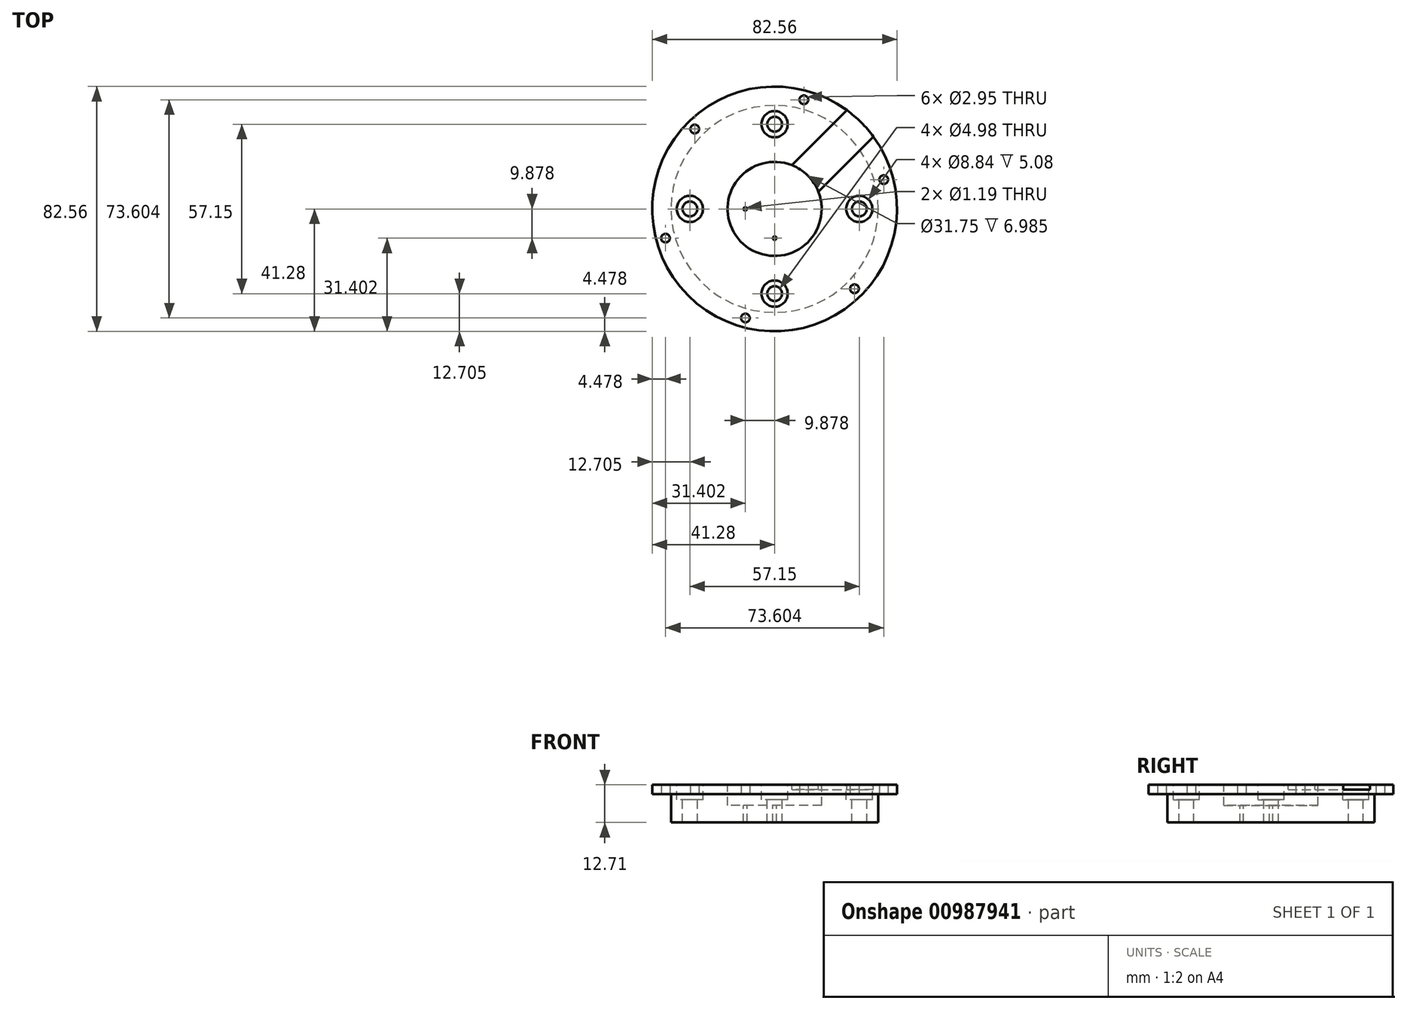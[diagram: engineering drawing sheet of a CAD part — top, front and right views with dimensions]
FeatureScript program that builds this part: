
annotation { "Feature Type Name" : "Feature", "Feature Type Description" : "" }
export const myFeature = defineFeature(function(context is Context, id is Id, definition is map)
    precondition{}
    {
        {
            var Q0;
            Q0=qCreatedBy(makeId("Top.planeOp"),FACE);
            var sketch = newSketch(context, id + "F0", { "sketchPlane" : qUnion([Q0])});
            skCircle(sketch, "E0", {"center": v(0, 0) * mm, "radius": 41.28 * mm});
            skSolve(sketch);
        }
        {
            var Q0;
            Q0 = qSketchRegion(id + "F0", true);
            extrude(context, id + "F1", {"entities" : qUnion([Q0]), "depth" : 3.17 * mm, "offsetDistance" : 25.4 * mm});
        }
        {
            var Q0;
            Q0=makeQuery(id+"F1.opExtrude","CAP_FACE",FACE,{"disambiguationData":[OSD([sQuery(id+"F0.wireOp",EDGE,"E0")])],"isStart":true});
            var sketch = newSketch(context, id + "F2", { "sketchPlane" : qUnion([Q0])});
            skCircle(sketch, "E1", {"center": v(0, 0) * mm, "radius": 34.93 * mm});
            skSolve(sketch);
        }
        {
            var Q0;
            Q0 = qSketchRegion(id + "F2", true);
            extrude(context, id + "F3", {"entities" : qUnion([Q0]), "operationType" : NewBodyOperationType.ADD, "depth" : 9.52 * mm, "offsetDistance" : 25.4 * mm});
        }
        {
            var Q0;
            Q0=makeQuery(id+"F1.opExtrude","CAP_FACE",FACE,{"disambiguationData":[OSD([sQuery(id+"F0.wireOp",EDGE,"E0")])],"isStart":false});
            var sketch = newSketch(context, id + "F4", { "sketchPlane" : qUnion([Q0])});
            skCircle(sketch, "E2", {"center": v(0, 28.58) * mm, "radius": 2.49 * mm});
            skCircle(sketch, "E3.1.0", {"center": v(-28.58, 0) * mm, "radius": 2.49 * mm});
            skCircle(sketch, "E3.2.0", {"center": v(0, -28.58) * mm, "radius": 2.49 * mm});
            skCircle(sketch, "E3.3.0", {"center": v(28.58, 0) * mm, "radius": 2.49 * mm});
            skPoint(sketch, "E3.center", {"position": v(0, 0) * mm});
            skSolve(sketch);
        }
        {
            var Q0;
            Q0 = qSketchRegion(id + "F4", true);
            extrude(context, id + "F5", {"entities" : qUnion([Q0]), "operationType" : NewBodyOperationType.REMOVE, "endBound" : BoundingType.UP_TO_NEXT, "oppositeDirection" : true, "depth" : 25.4 * mm, "offsetDistance" : 25.4 * mm});
        }
        {
            var Q0;
            Q0=makeQuery(id+"F1.opExtrude","CAP_FACE",FACE,{"disambiguationData":[OSD([sQuery(id+"F0.wireOp",EDGE,"E0")])],"isStart":false});
            var sketch = newSketch(context, id + "F6", { "sketchPlane" : qUnion([Q0])});
            skCircle(sketch, "E4", {"center": v(0, 28.58) * mm, "radius": 4.42 * mm});
            skCircle(sketch, "E5.1.0", {"center": v(-28.58, 0) * mm, "radius": 4.42 * mm});
            skCircle(sketch, "E5.2.0", {"center": v(0, -28.58) * mm, "radius": 4.42 * mm});
            skCircle(sketch, "E5.3.0", {"center": v(28.58, 0) * mm, "radius": 4.42 * mm});
            skPoint(sketch, "E5.center", {"position": v(0, 0) * mm});
            skSolve(sketch);
        }
        {
            var Q0;
            Q0 = qSketchRegion(id + "F6", true);
            extrude(context, id + "F7", {"entities" : qUnion([Q0]), "operationType" : NewBodyOperationType.REMOVE, "oppositeDirection" : true, "depth" : 5.08 * mm, "offsetDistance" : 25.4 * mm});
        }
        {
            var Q0;
            Q0=makeQuery(id+"F1.opExtrude","CAP_FACE",FACE,{"disambiguationData":[OSD([sQuery(id+"F0.wireOp",EDGE,"E0")])],"isStart":true});
            var sketch = newSketch(context, id + "F8", { "sketchPlane" : qUnion([Q0])});
            skPoint(sketch, "E6.center", {"position": v(0, 0) * mm});
            skCircle(sketch, "E7", {"center": v(9.86, -36.8) * mm, "radius": 1.47 * mm});
            skCircle(sketch, "E8.1.0", {"center": v(36.8, -9.86) * mm, "radius": 1.47 * mm});
            skCircle(sketch, "E8.2.0", {"center": v(26.94, 26.94) * mm, "radius": 1.47 * mm});
            skCircle(sketch, "E8.3.0", {"center": v(-9.86, 36.8) * mm, "radius": 1.47 * mm});
            skCircle(sketch, "E8.4.0", {"center": v(-36.8, 9.86) * mm, "radius": 1.47 * mm});
            skCircle(sketch, "E8.5.0", {"center": v(-26.94, -26.94) * mm, "radius": 1.47 * mm});
            skSolve(sketch);
        }
        {
            var Q0;
            Q0 = qSketchRegion(id + "F8", true);
            extrude(context, id + "F9", {"entities" : qUnion([Q0]), "operationType" : NewBodyOperationType.REMOVE, "endBound" : BoundingType.UP_TO_NEXT, "oppositeDirection" : true, "depth" : 25.4 * mm, "offsetDistance" : 25.4 * mm});
        }
        {
            var Q0;
            Q0=makeQuery(id+"F1.opExtrude","CAP_FACE",FACE,{"disambiguationData":[OSD([sQuery(id+"F0.wireOp",EDGE,"E0")])],"isStart":false});
            var sketch = newSketch(context, id + "F10", { "sketchPlane" : qUnion([Q0])});
            skCircle(sketch, "E9", {"center": v(0, 0) * mm, "radius": 15.88 * mm});
            skSolve(sketch);
        }
        {
            var Q0;
            Q0 = qSketchRegion(id + "F10", true);
            extrude(context, id + "F11", {"entities" : qUnion([Q0]), "operationType" : NewBodyOperationType.REMOVE, "oppositeDirection" : true, "depth" : 7 * mm, "offsetDistance" : 25.4 * mm});
        }
        {
            var Q0;
            Q0=makeQuery(id+"F11.boolean.opBoolean","COPY",FACE,{"derivedFrom":makeQuery(id+"F11.opExtrude","CAP_FACE",FACE,{"disambiguationData":[OSD([sQuery(id+"F10.wireOp",EDGE,"E9")])],"isStart":false})});
            var sketch = newSketch(context, id + "F12", { "sketchPlane" : qUnion([Q0])});
            skCircle(sketch, "E10", {"center": v(-9.88, 0) * mm, "radius": 0.6 * mm});
            skLineSegment(sketch, "E11", {"start": v(0, 0) * mm, "end": v(-11.23, -11.23) * mm, "construction": true});
            skLineSegment(sketch, "E12", {"start": v(-9.88, 0) * mm, "end": v(0, -9.88) * mm, "construction": true});
            skPoint(sketch, "E13", {"position": v(-4.94, -4.94) * mm});
            skCircle(sketch, "E14.MirrorC", {"center": v(0, -9.88) * mm, "radius": 0.6 * mm});
            skSolve(sketch);
        }
        {
            var Q0;
            Q0 = qSketchRegion(id + "F12", true);
            extrude(context, id + "F13", {"entities" : qUnion([Q0]), "operationType" : NewBodyOperationType.REMOVE, "endBound" : BoundingType.THROUGH_ALL, "oppositeDirection" : true, "depth" : 25.4 * mm, "offsetDistance" : 25.4 * mm});
        }
        {
            var Q0;
            Q0=makeQuery(id+"F1.opExtrude","CAP_FACE",FACE,{"disambiguationData":[OSD([sQuery(id+"F0.wireOp",EDGE,"E0")])],"isStart":false});
            var sketch = newSketch(context, id + "F14", { "sketchPlane" : qUnion([Q0])});
            skLineSegment(sketch, "E15", {"start": v(0, 0) * mm, "end": v(29.19, 29.19) * mm, "construction": true});
            skLineSegment(sketch, "E16", {"start": v(15.07, 24.05) * mm, "end": v(24.05, 15.07) * mm, "construction": true});
            skPoint(sketch, "E17", {"position": v(19.56, 19.56) * mm});
            skLineSegment(sketch, "E18", {"start": v(5.8, 14.78) * mm, "end": v(24.35, 33.33) * mm});
            skLineSegment(sketch, "E19", {"start": v(14.78, 5.8) * mm, "end": v(33.33, 24.35) * mm});
            skPoint(sketch, "E20", {"position": v(15.07, 24.05) * mm});
            skPoint(sketch, "E21", {"position": v(24.05, 15.07) * mm});
            skArc(sketch, "E22", {"start": v(24.35, 33.33) * mm, "mid": v(29.19, 29.19) * mm, "end": v(33.33, 24.35) * mm});
            skArc(sketch, "E23", {"start": v(5.8, 14.78) * mm, "mid": v(11.23, 11.23) * mm, "end": v(14.78, 5.8) * mm});
            skSolve(sketch);
        }
        {
            var Q0;
            Q0 = qSketchRegion(id + "F14", true);
            extrude(context, id + "F15", {"entities" : qUnion([Q0]), "operationType" : NewBodyOperationType.REMOVE, "oppositeDirection" : true, "depth" : 1.59 * mm, "offsetDistance" : 25.4 * mm});
        }
    });
